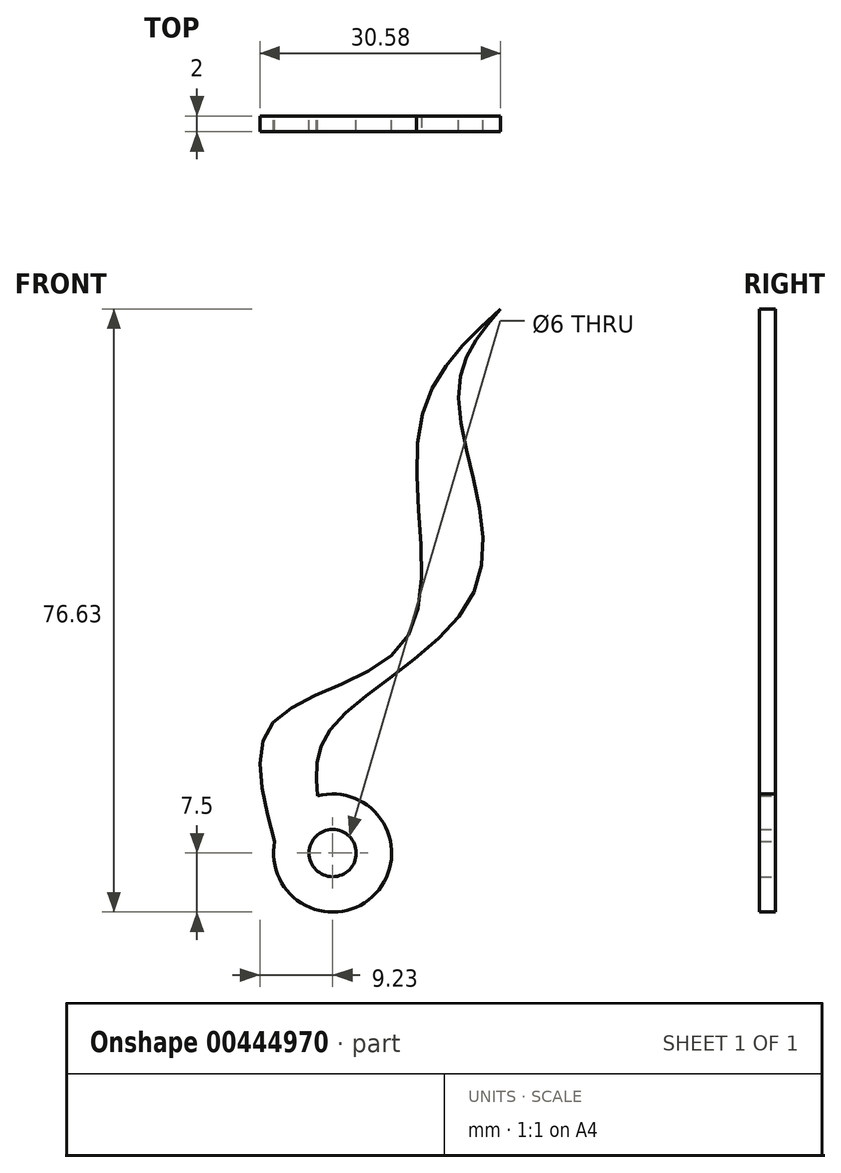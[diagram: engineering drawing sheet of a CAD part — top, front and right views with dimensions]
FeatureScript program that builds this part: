
annotation { "Feature Type Name" : "Feature", "Feature Type Description" : "" }
export const myFeature = defineFeature(function(context is Context, id is Id, definition is map)
    precondition{}
    {
        {
            var Q0;
            Q0=qCreatedBy(makeId("Front.planeOp"),FACE);
            var sketch = newSketch(context, id + "F0", { "sketchPlane" : qUnion([Q0])});
            skCircle(sketch, "E0", {"center": v(0, 0) * mm, "radius": 3 * mm});
            skArc(sketch, "E1", {"start": v(-7.35, 1.48) * mm, "mid": v(5.46, -5.14) * mm, "end": v(-1.93, 7.25) * mm});
            skFitSpline(sketch, "E2", {"points": [v(-7.35, 1.48) * mm, v(-7.5, 16.63) * mm, v(9.23, 27.02) * mm, v(10.96, 53.75) * mm, v(21.35, 69.13) * mm], "startDerivative": vector(-21.9, 79.86) * mm, "endDerivative": vector(57.65, 52.54) * mm});
            skFitSpline(sketch, "E3", {"points": [v(-1.93, 7.25) * mm, v(0, 16.06) * mm, v(18.27, 33.94) * mm, v(15.96, 58.17) * mm, v(21.35, 69.13) * mm], "startDerivative": vector(-3.66, 48.08) * mm, "endDerivative": vector(37.84, 43.95) * mm});
            skSolve(sketch);
        }
        {
            var Q0;
            Q0 = qSketchRegion(id + "F0", true);
            extrude(context, id + "F1", {"entities" : qUnion([Q0]), "depth" : 2 * mm});
        }
    });
